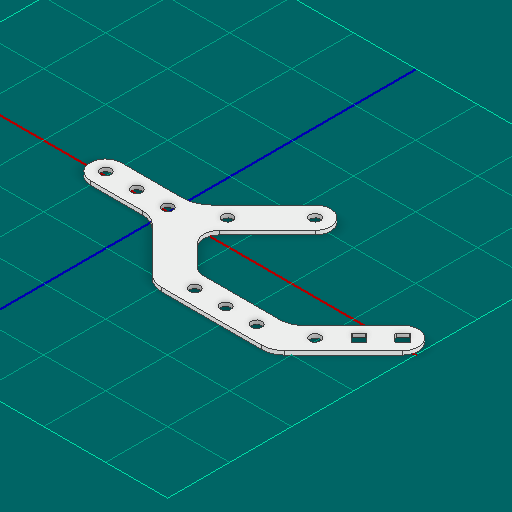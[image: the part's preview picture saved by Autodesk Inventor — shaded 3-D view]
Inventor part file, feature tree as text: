
AUTODESK INVENTOR PART (.ipt)
format: ipt  version: 2025 (Build 290162000, 162)  size: 185,856 bytes
history: native  units: in
note: dims shown in document units (in); Inventor stores cm internally (conversion verified against a paired STEP export)
features: other x3, extrude x1, sketch x1
ambient origin geometry x8: Origin, YZ Plane, XZ Plane, XY Plane, X Axis, Y Axis, Z Axis, Center Point
bodies: Solid1 (feature_tree)
feature tree (5):
  other  "Blocks"
  extrude  "Extrusion1"  TaperAngle=135.0deg  [1 undecoded]
  sketch  "Sketch1"  dims[d5=0.5in d6=135.0deg d7=0.375in d8=0.5in d9=0.375in d10=0.375in d11=0.5in d12=0.1875in d13=0.0625in d14=0.0in d15=1.25in d16=0.5in d17=45.0deg d18=0.25in d19=0.172in d20=0.25in d22=0.172in d23=0.5in d24=0.172in d25=0.5in]
  other  "main"
  other  "main:1"
note: 1 required parameter value undecoded (feature->parameter linkage not recoverable at this tier; creation-order binding heuristic only, values carry confidence <= 0.55)
